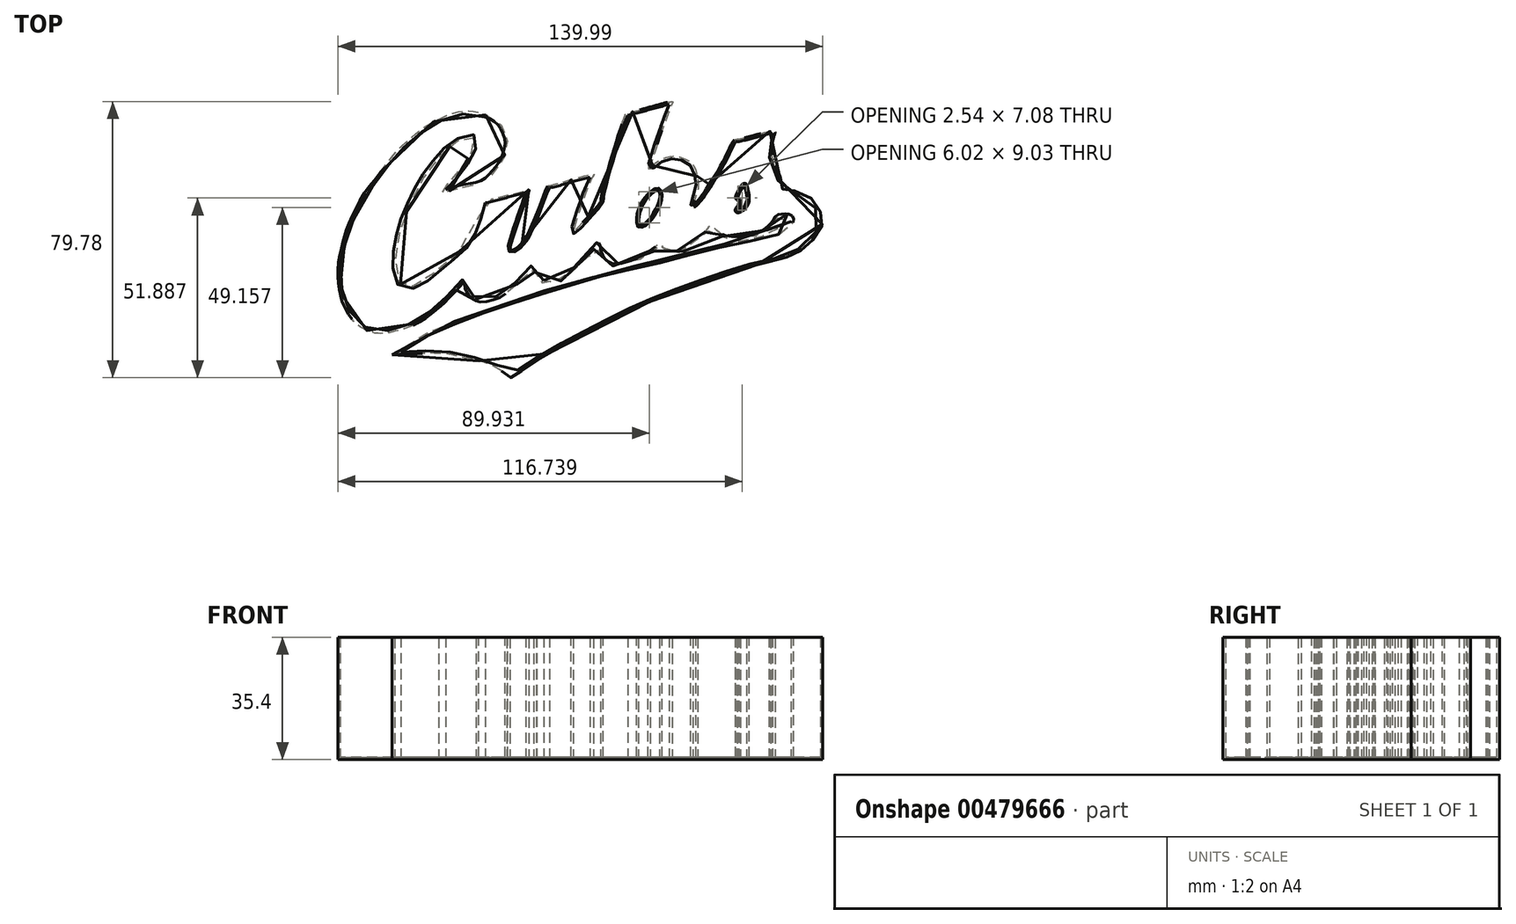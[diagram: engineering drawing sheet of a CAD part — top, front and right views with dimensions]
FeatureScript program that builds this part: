
annotation { "Feature Type Name" : "Feature", "Feature Type Description" : "" }
export const myFeature = defineFeature(function(context is Context, id is Id, definition is map)
    precondition{}
    {
        {
            var Q0;
            Q0=qCreatedBy(makeId("Top.planeOp"),FACE);
            var sketch = newSketch(context, id + "F0", { "sketchPlane" : qUnion([Q0])});
            skFitSpline(sketch, "E0", {"points": [v(16.61, 2.03) * mm, v(17.3, 3.94) * mm, v(18.09, 5.46) * mm, v(19.17, 6.76) * mm, v(20.56, 7.98) * mm, v(21.52, 8.58) * mm, v(22.08, 8.41) * mm, v(22.35, 7.85) * mm, v(22.35, 6.76) * mm, v(22.26, 5.67) * mm, v(21.91, 4.8) * mm, v(21.43, 3.72) * mm, v(20.65, 2.42) * mm, v(20, 1.11) * mm, v(19, 0) * mm, v(18, -0.97) * mm, v(17.4, -1.28) * mm, v(16.57, -1.45) * mm, v(16.35, -0.62) * mm, v(16.35, 0) * mm, v(16.44, 0.72) * mm, v(16.61, 2.03) * mm]});
            skFitSpline(sketch, "E1", {"points": [v(44.9, 6.6) * mm, v(46.83, 9.94) * mm, v(46.97, 9.66) * mm, v(47.3, 8.12) * mm, v(47.48, 6.88) * mm, v(47.5, 6.05) * mm, v(47.43, 5.36) * mm, v(47.1, 4.67) * mm, v(46.86, 4.1) * mm, v(46.46, 3.66) * mm, v(45.87, 3.2) * mm, v(45.43, 2.92) * mm, v(45.04, 2.78) * mm, v(44.83, 2.85) * mm, v(45.22, 3.38) * mm, v(45.61, 3.96) * mm, v(45.75, 4.62) * mm, v(45.82, 5.15) * mm, v(45.66, 5.73) * mm, v(45.36, 6.14) * mm, v(45.13, 6.44) * mm, v(44.9, 6.6) * mm]});
            skFitSpline(sketch, "E2", {"points": [v(-54.96, -38.97) * mm, v(-51.86, -36.92) * mm, v(-46.8, -33.71) * mm, v(-40.17, -30.62) * mm, v(-33.17, -27.8) * mm, v(-25.97, -25.2) * mm, v(-11.33, -20.54) * mm, v(-2.98, -17.98) * mm, v(5.37, -15.53) * mm, v(19.5, -12.3) * mm, v(30.08, -9.63) * mm, v(37.87, -7.63) * mm, v(50.7, -4.89) * mm, v(57.06, -3.2) * mm, v(59.03, -2) * mm, v(60.09, -0.66) * mm, v(60.37, 0) * mm, v(59.98, 0.85) * mm, v(59.14, 1.13) * mm, v(57.7, 1.06) * mm, v(56.46, 0.85) * mm, v(55.9, 0) * mm, v(54.77, -1.58) * mm, v(52.3, -3.62) * mm, v(49.6, -4.81) * mm, v(47.7, -5.27) * mm, v(44.64, -5.48) * mm, v(41.64, -5.2) * mm, v(39.64, -4.46) * mm, v(38.3, -3.55) * mm, v(37.1, -2.35) * mm, v(36.79, -2.77) * mm, v(33.66, -5.87) * mm, v(29.84, -8.68) * mm, v(27.41, -9.5) * mm, v(25.8, -9.64) * mm, v(24.27, -9.47) * mm, v(23.13, -8.9) * mm, v(22.2, -7.6) * mm, v(22, -7.84) * mm, v(20.94, -8.74) * mm, v(18.96, -10.03) * mm, v(17.16, -11.05) * mm, v(15.86, -11.75) * mm, v(13.93, -12.5) * mm, v(10.7, -13.32) * mm, v(8.53, -13.18) * mm, v(6.9, -12.36) * mm, v(5.88, -11.5) * mm, v(5.06, -9.85) * mm, v(4.74, -8.93) * mm, v(4.5, -7.67) * mm, v(4.38, -7.14) * mm, v(3.69, -7.92) * mm, v(2.27, -9.82) * mm, v(0.8, -11.46) * mm, v(-0.77, -13.13) * mm, v(-3.77, -15.94) * mm, v(-5.43, -17.15) * mm, v(-6.92, -18) * mm, v(-9.21, -18.58) * mm, v(-11.05, -18.18) * mm, v(-11.27, -18.18) * mm, v(-12.06, -17.63) * mm, v(-12.82, -16.92) * mm, v(-13.38, -16.13) * mm, v(-13.6, -15.5) * mm, v(-13.78, -14.92) * mm, v(-13.92, -14.45) * mm, v(-13.92, -13.8) * mm, v(-13.92, -13.57) * mm, v(-14.21, -13.62) * mm, v(-14.9, -14.53) * mm, v(-15.67, -15.47) * mm, v(-16.56, -16.4) * mm, v(-17.78, -17.6) * mm, v(-19.15, -18.85) * mm, v(-20.07, -19.63) * mm, v(-22.69, -21.7) * mm, v(-26.4, -23.3) * mm, v(-29.89, -23.6) * mm, v(-31.5, -22.82) * mm, v(-32.86, -21.7) * mm, v(-33.47, -20.49) * mm, v(-33.86, -19.6) * mm, v(-34.02, -18.48) * mm, v(-34.13, -17.77) * mm, v(-34.36, -17.98) * mm, v(-35.14, -18.96) * mm, v(-37.17, -21.2) * mm, v(-38.74, -22.82) * mm, v(-40.6, -24.6) * mm, v(-42.94, -26.51) * mm, v(-46.16, -28.95) * mm, v(-49.99, -30.9) * mm, v(-53.58, -32.02) * mm, v(-57.06, -32.72) * mm, v(-60.06, -32.6) * mm, v(-62.42, -31.84) * mm, v(-65.13, -30.13) * mm, v(-67.19, -27.77) * mm, v(-68.6, -25.18) * mm, v(-69.37, -23.42) * mm, v(-70.13, -20.23) * mm, v(-70.56, -16.48) * mm, v(-70.3, -11.74) * mm, v(-69.34, -7.21) * mm, v(-68.34, -3.55) * mm, v(-66.51, 0.95) * mm, v(-63.23, 7.37) * mm, v(-59.4, 12.4) * mm, v(-54.37, 18.95) * mm, v(-50.32, 23) * mm, v(-45, 27.24) * mm, v(-41.35, 29.22) * mm, v(-37.9, 30.7) * mm, v(-34.05, 31.48) * mm, v(-30.6, 31.33) * mm, v(-27.85, 30.45) * mm], "startDerivative": vector(290.45, 190.87) * mm, "endDerivative": vector(300.32, -116.55) * mm});
            skPoint(sketch, "E3.28.internal.snap0", {"position": v(-71.72, -5.7) * mm});
            skPoint(sketch, "E3.87.internal.snap0", {"position": v(-71.72, -5.7) * mm});
            skFitSpline(sketch, "E3", {"points": [v(-27.85, 30.45) * mm, v(-25.19, 29.22) * mm, v(-23.31, 27.34) * mm, v(-22.23, 25.17) * mm, v(-21.64, 23.15) * mm, v(-21.79, 20.6) * mm, v(-22.38, 18.77) * mm, v(-23.8, 15.81) * mm, v(-26.27, 12.9) * mm, v(-28.83, 10.79) * mm, v(-34.19, 9.58) * mm, v(-40.88, 7.8) * mm, v(-41.28, 7.84) * mm, v(-40.7, 8.66) * mm, v(-37.8, 11.54) * mm, v(-35.48, 14.16) * mm, v(-33.63, 16.68) * mm, v(-32.45, 18.45) * mm, v(-31.44, 20.72) * mm, v(-30.6, 22.24) * mm, v(-31.5, 23.95) * mm, v(-32.72, 24.07) * mm, v(-35.77, 22.97) * mm, v(-38.94, 20.72) * mm, v(-42.17, 17.18) * mm, v(-45.76, 12.37) * mm, v(-48.5, 7.37) * mm, v(-51.77, 0) * mm, v(-53.18, -5.7) * mm, v(-54.04, -12.62) * mm, v(-53.18, -16.91) * mm, v(-52.32, -18.79) * mm, v(-50.91, -19.18) * mm, v(-48.41, -18.86) * mm, v(-44.5, -16.6) * mm, v(-39.51, -12.3) * mm, v(-32.17, -4.96) * mm, v(-28.58, 5.43) * mm, v(-27.85, 5.72) * mm, v(-15.46, 8.77) * mm, v(-15.4, 8.44) * mm, v(-20.7, -7.4) * mm, v(-20.76, -8.38) * mm, v(-20.5, -8.7) * mm, v(-19.32, -8.31) * mm, v(-17.69, -6.8) * mm, v(-16.31, -5.04) * mm, v(-12.9, 2.55) * mm, v(-10.03, 9.82) * mm, v(-9.18, 10.08) * mm, v(3.26, 13.35) * mm, v(2.93, 12.37) * mm, v(-2.5, -3.2) * mm, v(-2.04, -2.94) * mm, v(5.16, 5.04) * mm, v(5.38, 6.29) * mm, v(12.4, 30.45) * mm, v(13.5, 31.12) * mm, v(25.95, 34.26) * mm, v(25.86, 33.49) * mm, v(19.69, 15.3) * mm, v(20.46, 15.99) * mm, v(23.63, 17.87) * mm, v(26.63, 18.47) * mm, v(29.3, 17.79) * mm, v(31.6, 16.41) * mm, v(32.98, 13.67) * mm, v(33.5, 9.98) * mm, v(32.81, 7.15) * mm, v(32.04, 4.23) * mm, v(32.73, 4.92) * mm, v(34.44, 6.98) * mm, v(37.1, 11.1) * mm, v(41.13, 17.96) * mm, v(43.8, 23.1) * mm, v(45.34, 23.45) * mm, v(55.72, 25.85) * mm, v(55.72, 25.34) * mm, v(55.03, 23.02) * mm, v(54.6, 19.93) * mm, v(55.65, 15.16) * mm, v(56.96, 12.9) * mm, v(57.76, 9.03) * mm, v(58.86, 8.74) * mm, v(64.77, 7.28) * mm, v(68.35, 3.2) * mm, v(69.37, -0.97) * mm, v(66.6, -5.7) * mm, v(62.8, -8.92) * mm, v(58.2, -11.04) * mm, v(50.2, -12.95) * mm, v(39.36, -16.3) * mm, v(25.57, -21.18) * mm, v(15.42, -25.43) * mm, v(4.38, -30.9) * mm, v(-6.97, -36.9) * mm, v(-17.37, -43.36) * mm, v(-20.47, -45.5) * mm, v(-21.43, -45.15) * mm, v(-25.61, -42.16) * mm, v(-34.05, -39.77) * mm, v(-40.6, -38.58) * mm, v(-49.99, -38.7) * mm, v(-54.96, -38.97) * mm], "startDerivative": vector(351.22, -133.42) * mm, "endDerivative": vector(-427.9, -24.28) * mm});
            skSolve(sketch);
        }
        {
            var Q0;
            Q0=makeQuery(id+"F0.imprint","IMPRINT",FACE,{"disambiguationData":[TD([[makeQuery(id+"F0.imprint","IMPRINT",EDGE,{"derivedFrom":sQuery(id+"F0.wireOp",EDGE,"E0")}),1.0]])]});
            extrude(context, id + "F1", {"entities" : qUnion([Q0]), "depth" : 25.4 * mm});
        }
        {
            var Q0;
            Q0=makeQuery(id+"F1.opExtrude","CAP_FACE",FACE,{"disambiguationData":[OSD([sQuery(id+"F0.wireOp",EDGE,"E0"),sQuery(id+"F0.wireOp",EDGE,"E1"),sQuery(id+"F0.wireOp",EDGE,"E2"),sQuery(id+"F0.wireOp",EDGE,"E3")])],"isStart":false});
            extrude(context, id + "F2", {"entities" : qUnion([Q0]), "operationType" : NewBodyOperationType.ADD, "depth" : 10 * mm});
        }
        {
            var Q0;
            Q0=makeQuery(id+"F2.opExtrude","CAP_FACE",FACE,{"disambiguationData":[OSD([sQuery(id+"F0.wireOp",EDGE,"E0"),sQuery(id+"F0.wireOp",EDGE,"E1"),sQuery(id+"F0.wireOp",EDGE,"E2"),sQuery(id+"F0.wireOp",EDGE,"E3")])],"isStart":false});
            shell(context, id + "F3", {"entities" : qUnion([Q0]), "thickness" : 0.7 * mm});
        }
    });
